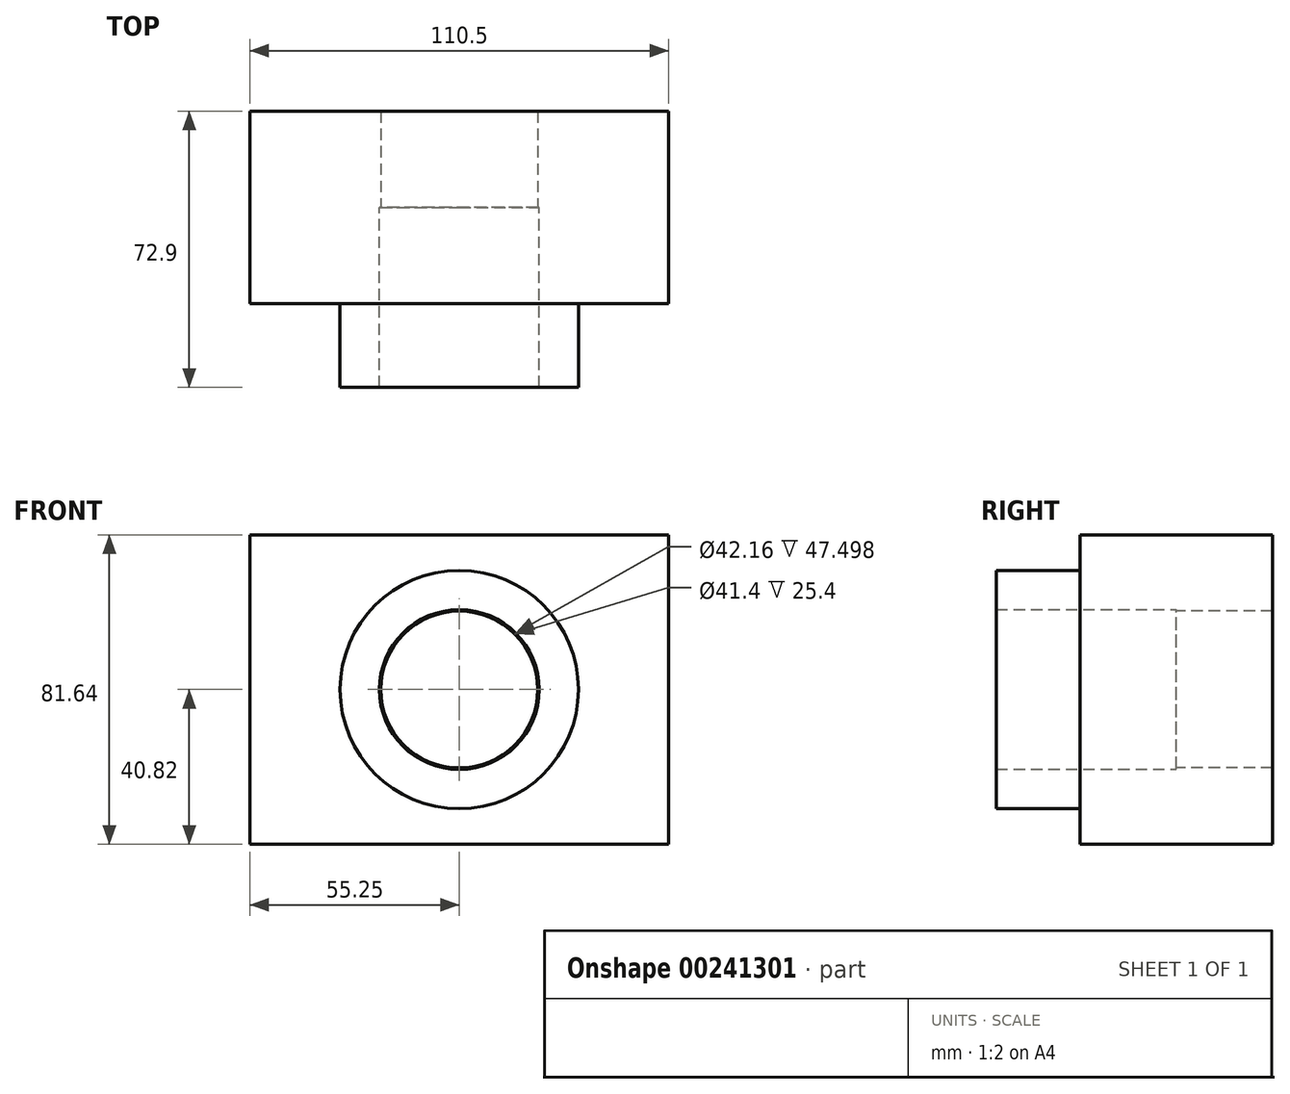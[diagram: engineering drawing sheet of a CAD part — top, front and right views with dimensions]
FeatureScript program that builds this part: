
annotation { "Feature Type Name" : "Feature", "Feature Type Description" : "" }
export const myFeature = defineFeature(function(context is Context, id is Id, definition is map)
    precondition{}
    {
        {
            var Q0;
            Q0=qCreatedBy(makeId("Front.planeOp"),FACE);
            var sketch = newSketch(context, id + "F0", { "sketchPlane" : qUnion([Q0])});
            skLineSegment(sketch, "E0.bottom", {"start": v(55.25, -40.82) * mm, "end": v(-55.25, -40.82) * mm});
            skLineSegment(sketch, "E0.top", {"start": v(55.25, 40.82) * mm, "end": v(-55.25, 40.82) * mm});
            skLineSegment(sketch, "E0.left", {"start": v(55.25, -40.82) * mm, "end": v(55.25, 40.82) * mm});
            skLineSegment(sketch, "E0.right", {"start": v(-55.25, -40.82) * mm, "end": v(-55.25, 40.82) * mm});
            skPoint(sketch, "E0.middle", {"position": v(0, 0) * mm});
            skSolve(sketch);
        }
        {
            var Q0;
            Q0=makeQuery(id+"F0.imprint","IMPRINT",FACE,{"disambiguationData":[TD([[makeQuery(id+"F0.imprint","IMPRINT",EDGE,{"derivedFrom":sQuery(id+"F0.wireOp",EDGE,"E0.bottom")}),-1.0]])]});
            extrude(context, id + "F1", {"entities" : qUnion([Q0]), "depth" : 25.4 * mm});
        }
        {
            var Q0;
            Q0=makeQuery(id+"F1.opExtrude","CAP_FACE",FACE,{"disambiguationData":[OSD([sQuery(id+"F0.wireOp",EDGE,"E0.bottom"),sQuery(id+"F0.wireOp",EDGE,"E0.top"),sQuery(id+"F0.wireOp",EDGE,"E0.left"),sQuery(id+"F0.wireOp",EDGE,"E0.right")])],"isStart":true});
            extrude(context, id + "F2", {"entities" : qUnion([Q0]), "operationType" : NewBodyOperationType.ADD, "depth" : 25.4 * mm});
        }
        {
            var Q0;
            Q0=qCreatedBy(makeId("Front.planeOp"),FACE);
            var sketch = newSketch(context, id + "F3", { "sketchPlane" : qUnion([Q0])});
            skCircle(sketch, "E1", {"center": v(0, 0) * mm, "radius": 21.08 * mm});
            skSolve(sketch);
        }
        {
            var Q0;
            Q0=qCreatedBy(makeId("Front.planeOp"),FACE);
            var sketch = newSketch(context, id + "F4", { "sketchPlane" : qUnion([Q0])});
            skCircle(sketch, "E2", {"center": v(0, 0) * mm, "radius": 31.45 * mm});
            skSolve(sketch);
        }
        {
            var Q0;
            Q0 = qSketchRegion(id + "F4", true);
            extrude(context, id + "F5", {"entities" : qUnion([Q0]), "operationType" : NewBodyOperationType.ADD, "depth" : 47.5 * mm});
        }
        {
            var Q0;
            Q0 = qSketchRegion(id + "F3", true);
            extrude(context, id + "F6", {"entities" : qUnion([Q0]), "operationType" : NewBodyOperationType.REMOVE, "depth" : 117.86 * mm});
        }
        {
            var Q0;
            Q0=qCreatedBy(makeId("Front.planeOp"),FACE);
            var sketch = newSketch(context, id + "F7", { "sketchPlane" : qUnion([Q0])});
            skCircle(sketch, "E3", {"center": v(0, 0) * mm, "radius": 20.7 * mm});
            skSolve(sketch);
        }
        {
            var Q0;
            Q0 = qSketchRegion(id + "F7", true);
            extrude(context, id + "F8", {"entities" : qUnion([Q0]), "operationType" : NewBodyOperationType.REMOVE, "oppositeDirection" : true, "depth" : 81.53 * mm});
        }
    });
